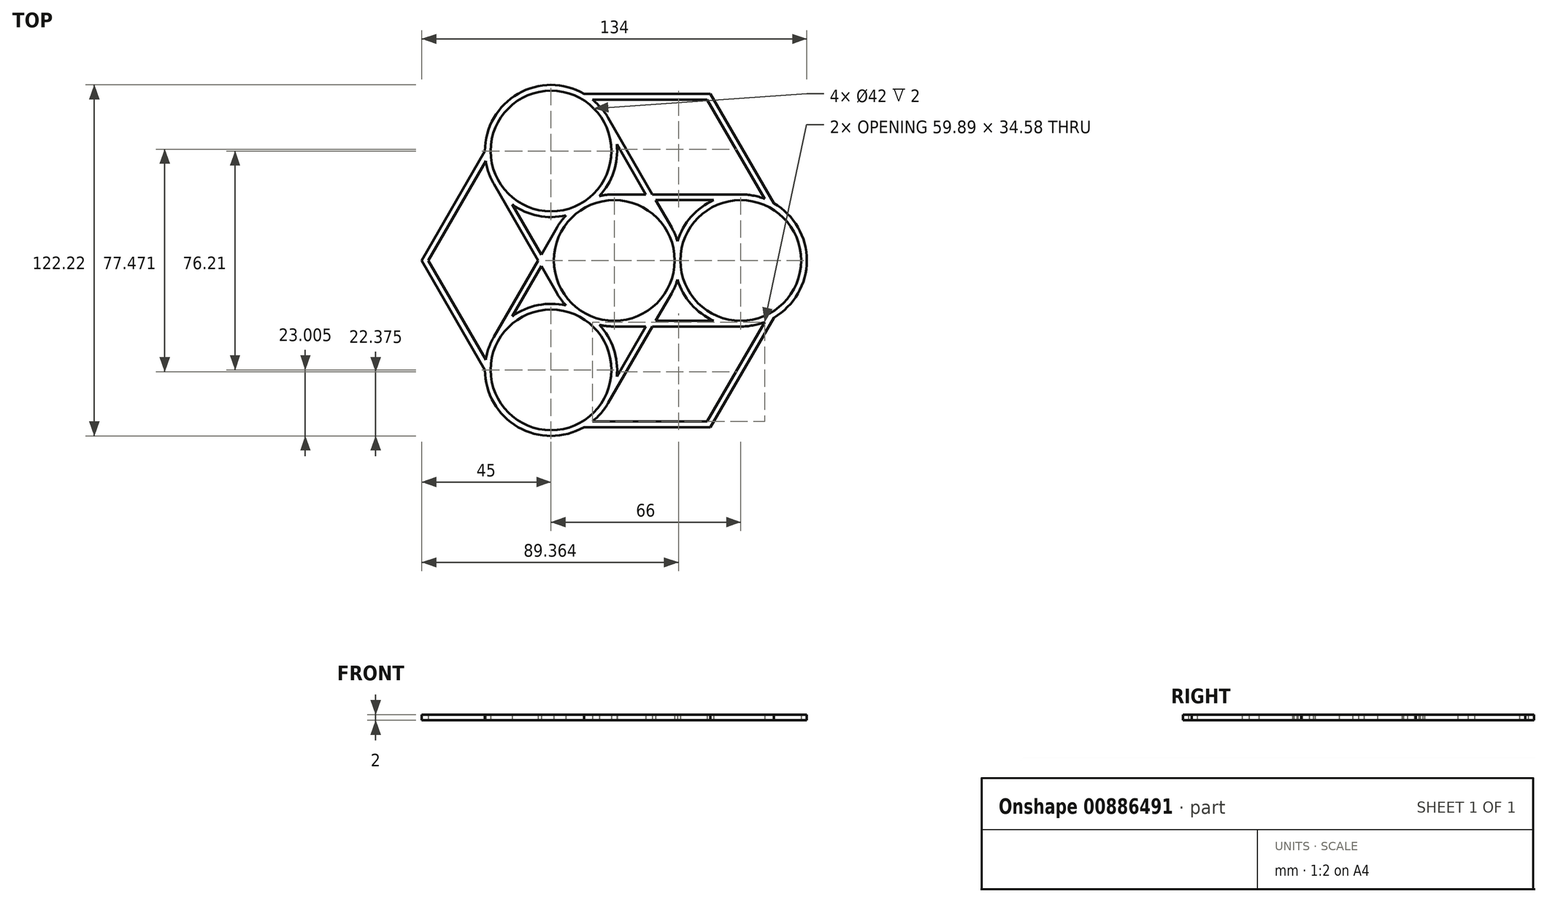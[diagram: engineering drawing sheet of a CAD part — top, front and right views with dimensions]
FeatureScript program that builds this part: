
annotation { "Feature Type Name" : "Feature", "Feature Type Description" : "" }
export const myFeature = defineFeature(function(context is Context, id is Id, definition is map)
    precondition{}
    {
        {
            var Q0;
            Q0=qCreatedBy(makeId("Top.planeOp"),FACE);
            var sketch = newSketch(context, id + "F0", { "sketchPlane" : qUnion([Q0])});
            skArc(sketch, "E0", {"start": v(0, 23) * mm, "mid": v(-2.61, 22.85) * mm, "end": v(-5.2, 22.4) * mm});
            skArc(sketch, "E1", {"start": v(34.62, 21) * mm, "mid": v(26.76, 15.22) * mm, "end": v(22, 6.7) * mm});
            skCircle(sketch, "E2", {"center": v(0, 0) * mm, "radius": 21 * mm});
            skCircle(sketch, "E3", {"center": v(44, 0) * mm, "radius": 21 * mm});
            skLineSegment(sketch, "E4", {"start": v(0, 23) * mm, "end": v(10.97, 23) * mm});
            skLineSegment(sketch, "E5", {"start": v(9.38, -21) * mm, "end": v(12.12, -21) * mm});
            skLineSegment(sketch, "E6", {"start": v(0, -23) * mm, "end": v(10.97, -23) * mm});
            skLineSegment(sketch, "E7", {"start": v(9.38, 21) * mm, "end": v(12.12, 21) * mm});
            skArc(sketch, "E8.trimOffspring", {"start": v(19.92, -11.5) * mm, "mid": v(21.1, -9.16) * mm, "end": v(22, -6.7) * mm});
            skArc(sketch, "E9.trimOffspring", {"start": v(44, -23) * mm, "mid": v(48.23, -22.6) * mm, "end": v(52.3, -21.45) * mm});
            skArc(sketch, "E10.trimOffspring", {"start": v(22, -6.7) * mm, "mid": v(26.76, -15.22) * mm, "end": v(34.62, -21) * mm});
            skArc(sketch, "E11.trimOffspring", {"start": v(22, 6.7) * mm, "mid": v(21.1, 9.16) * mm, "end": v(19.92, 11.5) * mm});
            skLineSegment(sketch, "E12.1.1", {"start": v(13.5, 18.62) * mm, "end": v(12.12, 21) * mm});
            skArc(sketch, "E12.1.2", {"start": v(-5.2, 22.4) * mm, "mid": v(-0.2, 30.79) * mm, "end": v(0.88, 40.48) * mm});
            skLineSegment(sketch, "E12.1.3", {"start": v(-22.88, -2.38) * mm, "end": v(-24.25, 0) * mm});
            skArc(sketch, "E12.1.4", {"start": v(-35.5, 19.48) * mm, "mid": v(-26.56, 15.56) * mm, "end": v(-16.8, 15.7) * mm});
            skArc(sketch, "E12.1.5", {"start": v(-19.92, -11.5) * mm, "mid": v(-18.48, -13.69) * mm, "end": v(-16.8, -15.7) * mm});
            skLineSegment(sketch, "E12.1.6", {"start": v(-19.92, -11.5) * mm, "end": v(-25.4, -2) * mm});
            skLineSegment(sketch, "E12.1.7", {"start": v(19.92, 11.5) * mm, "end": v(14.43, 21) * mm});
            skCircle(sketch, "E12.1.8", {"center": v(-22, 38.1) * mm, "radius": 21 * mm});
            skArc(sketch, "E12.1.10", {"start": v(-2.08, 49.6) * mm, "mid": v(-4.53, 53.07) * mm, "end": v(-7.58, 56.02) * mm});
            skLineSegment(sketch, "E12.2.1", {"start": v(-22.88, 2.38) * mm, "end": v(-24.25, 0) * mm});
            skArc(sketch, "E12.2.2", {"start": v(-16.8, -15.7) * mm, "mid": v(-26.56, -15.56) * mm, "end": v(-35.5, -19.48) * mm});
            skLineSegment(sketch, "E12.2.3", {"start": v(13.5, -18.62) * mm, "end": v(12.12, -21) * mm});
            skArc(sketch, "E12.2.4", {"start": v(0.88, -40.48) * mm, "mid": v(-0.2, -30.79) * mm, "end": v(-5.2, -22.4) * mm});
            skLineSegment(sketch, "E12.2.6", {"start": v(19.92, -11.5) * mm, "end": v(14.43, -21) * mm});
            skLineSegment(sketch, "E12.2.7", {"start": v(-19.92, 11.5) * mm, "end": v(-25.4, 2) * mm});
            skCircle(sketch, "E12.2.8", {"center": v(-22, -38.1) * mm, "radius": 21 * mm});
            skArc(sketch, "E12.2.9", {"start": v(-5.2, -22.4) * mm, "mid": v(-2.61, -22.85) * mm, "end": v(0, -23) * mm});
            skArc(sketch, "E12.2.10", {"start": v(-41.92, -26.6) * mm, "mid": v(-43.7, -30.46) * mm, "end": v(-44.73, -34.58) * mm});
            skArc(sketch, "E12.2.11", {"start": v(-22.88, 2.38) * mm, "mid": v(-23, 0) * mm, "end": v(-22.88, -2.38) * mm});
            skLineSegment(sketch, "E13.trimOffspring", {"start": v(10.97, 23) * mm, "end": v(0.88, 40.48) * mm});
            skLineSegment(sketch, "E14.trimOffspring", {"start": v(13.28, 23) * mm, "end": v(-2.08, 49.6) * mm});
            skLineSegment(sketch, "E15.trimOffspring", {"start": v(13.28, 23) * mm, "end": v(44, 23) * mm});
            skLineSegment(sketch, "E16.trimOffspring", {"start": v(14.43, 21) * mm, "end": v(34.62, 21) * mm});
            skArc(sketch, "E17.trimOffspring", {"start": v(-16.8, 15.7) * mm, "mid": v(-18.48, 13.69) * mm, "end": v(-19.92, 11.5) * mm});
            skLineSegment(sketch, "E18.trimOffspring", {"start": v(-25.4, 2) * mm, "end": v(-35.5, 19.48) * mm});
            skLineSegment(sketch, "E19.trimOffspring", {"start": v(-26.56, 0) * mm, "end": v(-41.92, -26.6) * mm});
            skLineSegment(sketch, "E20.trimOffspring", {"start": v(-26.56, 0) * mm, "end": v(-41.92, 26.6) * mm});
            skLineSegment(sketch, "E21.trimOffspring", {"start": v(-25.4, -2) * mm, "end": v(-35.5, -19.48) * mm});
            skArc(sketch, "E22.trimOffspring", {"start": v(9.38, -21) * mm, "mid": v(11.5, -19.92) * mm, "end": v(13.5, -18.62) * mm});
            skLineSegment(sketch, "E23.trimOffspring", {"start": v(10.97, -23) * mm, "end": v(0.88, -40.48) * mm});
            skLineSegment(sketch, "E24.trimOffspring", {"start": v(13.28, -23) * mm, "end": v(-2.08, -49.6) * mm});
            skLineSegment(sketch, "E25.trimOffspring", {"start": v(14.43, -21) * mm, "end": v(34.62, -21) * mm});
            skLineSegment(sketch, "E26.trimOffspring", {"start": v(13.28, -23) * mm, "end": v(44, -23) * mm});
            skArc(sketch, "E27.trimOffspring", {"start": v(13.5, 18.62) * mm, "mid": v(11.5, 19.92) * mm, "end": v(9.38, 21) * mm});
            skCircle(sketch, "E28.cCircle", {"center": v(0, 0) * mm, "radius": 67 * mm, "construction": true});
            skLineSegment(sketch, "E28.0", {"start": v(-33.5, 58.02) * mm, "end": v(33.5, 58.02) * mm, "construction": true});
            skLineSegment(sketch, "E28.1", {"start": v(33.5, 58.02) * mm, "end": v(67, 0) * mm, "construction": true});
            skLineSegment(sketch, "E28.2", {"start": v(67, 0) * mm, "end": v(33.5, -58.02) * mm, "construction": true});
            skLineSegment(sketch, "E28.3", {"start": v(33.5, -58.02) * mm, "end": v(-33.5, -58.02) * mm, "construction": true});
            skLineSegment(sketch, "E28.4", {"start": v(-33.5, -58.02) * mm, "end": v(-67, 0) * mm, "construction": true});
            skLineSegment(sketch, "E28.5", {"start": v(-67, 0) * mm, "end": v(-33.5, 58.02) * mm, "construction": true});
            skLineSegment(sketch, "E29", {"start": v(33.5, -58.02) * mm, "end": v(55.5, -19.92) * mm});
            skLineSegment(sketch, "E30", {"start": v(33.5, 58.02) * mm, "end": v(55.5, 19.92) * mm});
            skLineSegment(sketch, "E31", {"start": v(33.5, 58.02) * mm, "end": v(-10.5, 58.02) * mm});
            skLineSegment(sketch, "E32", {"start": v(-67, 0) * mm, "end": v(-45, 38.1) * mm});
            skLineSegment(sketch, "E33", {"start": v(-67, 0) * mm, "end": v(-45, -38.1) * mm});
            skLineSegment(sketch, "E34", {"start": v(33.5, -58.02) * mm, "end": v(-10.5, -58.02) * mm});
            skLineSegment(sketch, "E35", {"start": v(32.35, -56.02) * mm, "end": v(52.3, -21.45) * mm});
            skLineSegment(sketch, "E36", {"start": v(32.35, -56.02) * mm, "end": v(-7.58, -56.02) * mm});
            skArc(sketch, "E37.trimOffspring", {"start": v(55.5, -19.92) * mm, "mid": v(67, 0) * mm, "end": v(55.5, 19.92) * mm});
            skArc(sketch, "E38.trimOffspring", {"start": v(-7.58, -56.02) * mm, "mid": v(-4.53, -53.07) * mm, "end": v(-2.08, -49.6) * mm});
            skLineSegment(sketch, "E39", {"start": v(52.3, 21.45) * mm, "end": v(32.35, 56.02) * mm});
            skLineSegment(sketch, "E40", {"start": v(32.35, 56.02) * mm, "end": v(-7.58, 56.02) * mm});
            skArc(sketch, "E41.trimOffspring", {"start": v(52.3, 21.45) * mm, "mid": v(48.23, 22.6) * mm, "end": v(44, 23) * mm});
            skArc(sketch, "E42.trimOffspring", {"start": v(-10.5, 58.02) * mm, "mid": v(-33.5, 58.02) * mm, "end": v(-45, 38.1) * mm});
            skLineSegment(sketch, "E43", {"start": v(-44.73, -34.58) * mm, "end": v(-64.7, 0) * mm});
            skLineSegment(sketch, "E44", {"start": v(-64.7, 0) * mm, "end": v(-44.73, 34.58) * mm});
            skArc(sketch, "E45.trimOffspring", {"start": v(-45, -38.1) * mm, "mid": v(-33.5, -58.02) * mm, "end": v(-10.5, -58.02) * mm});
            skArc(sketch, "E46.trimOffspring", {"start": v(-44.73, 34.58) * mm, "mid": v(-43.7, 30.46) * mm, "end": v(-41.92, 26.6) * mm});
            skSolve(sketch);
        }
        {
            var Q0;
            Q0=makeQuery(id+"F0.imprint","IMPRINT",FACE,{"disambiguationData":[TD([[makeQuery(id+"F0.imprint","IMPRINT",EDGE,{"derivedFrom":sQuery(id+"F0.wireOp",EDGE,"E0")}),1.0]])]});
            var Q1;
            Q1=makeQuery(id+"F0.imprint","IMPRINT",FACE,{"disambiguationData":[TD([[makeQuery(id+"F0.imprint","IMPRINT",EDGE,{"derivedFrom":sQuery(id+"F0.wireOp",EDGE,"E5")}),1.0]])]});
            var Q2;
            Q2=makeQuery(id+"F0.imprint","IMPRINT",FACE,{"disambiguationData":[TD([[makeQuery(id+"F0.imprint","IMPRINT",EDGE,{"derivedFrom":sQuery(id+"F0.wireOp",EDGE,"E7")}),-1.0]])]});
            var Q3;
            Q3=makeQuery(id+"F0.imprint","IMPRINT",FACE,{"disambiguationData":[TD([[makeQuery(id+"F0.imprint","IMPRINT",EDGE,{"derivedFrom":sQuery(id+"F0.wireOp",EDGE,"E12.1.3")}),-1.0]])]});
            extrude(context, id + "F1", {"entities" : qUnion([Q0, Q1, Q2, Q3]), "depth" : 2 * mm, "offsetDistance" : 25 * mm});
        }
    });
